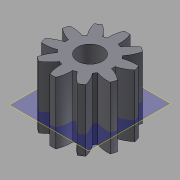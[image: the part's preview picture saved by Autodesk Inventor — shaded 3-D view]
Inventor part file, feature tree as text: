
AUTODESK INVENTOR PART (.ipt)
format: ipt  version: 2015 (Build 190159000, 159)  size: 166,912 bytes
history: native  units: in
note: dims shown in document units (in); Inventor stores cm internally (conversion verified against a paired STEP export)
features: other x13, sketch x3, plane x2
ambient origin geometry x8: Origin, YZ Plane, XZ Plane, XY Plane, X Axis, Y Axis, Z Axis, Center Point
bodies: Solid1 (feature_tree)
feature tree (18):
  other  "Spur Gear19_MIR4.ipt"
  other  "Solid1::Spur Gear19_MIR4.ipt"
  other  "TaggingFeature1"
  sketch  "Sketch1"  dims[d0=0.3937in]
  sketch  "Sketch2"  dims[d16=0.4724in d17=0.0in d41=0.0in d43=0.4724in d46=0.4724in d47=0.0in d48=0.0in]
  sketch  "Sketch3"
  plane  "XZ Plane_1"
  plane  "Work Plane2"
  other  "Z Axis_1"
  other  "Srf1"
  other  "Srf1::Derived"
  other  "Distance iMate"
  other  "Align iMate"
  other  "Mesh iMate"
  other  "Axis iMate"
  other  "Position iMate"
  other  "Mesh iMate2"
  other  "Start plane iMate"
